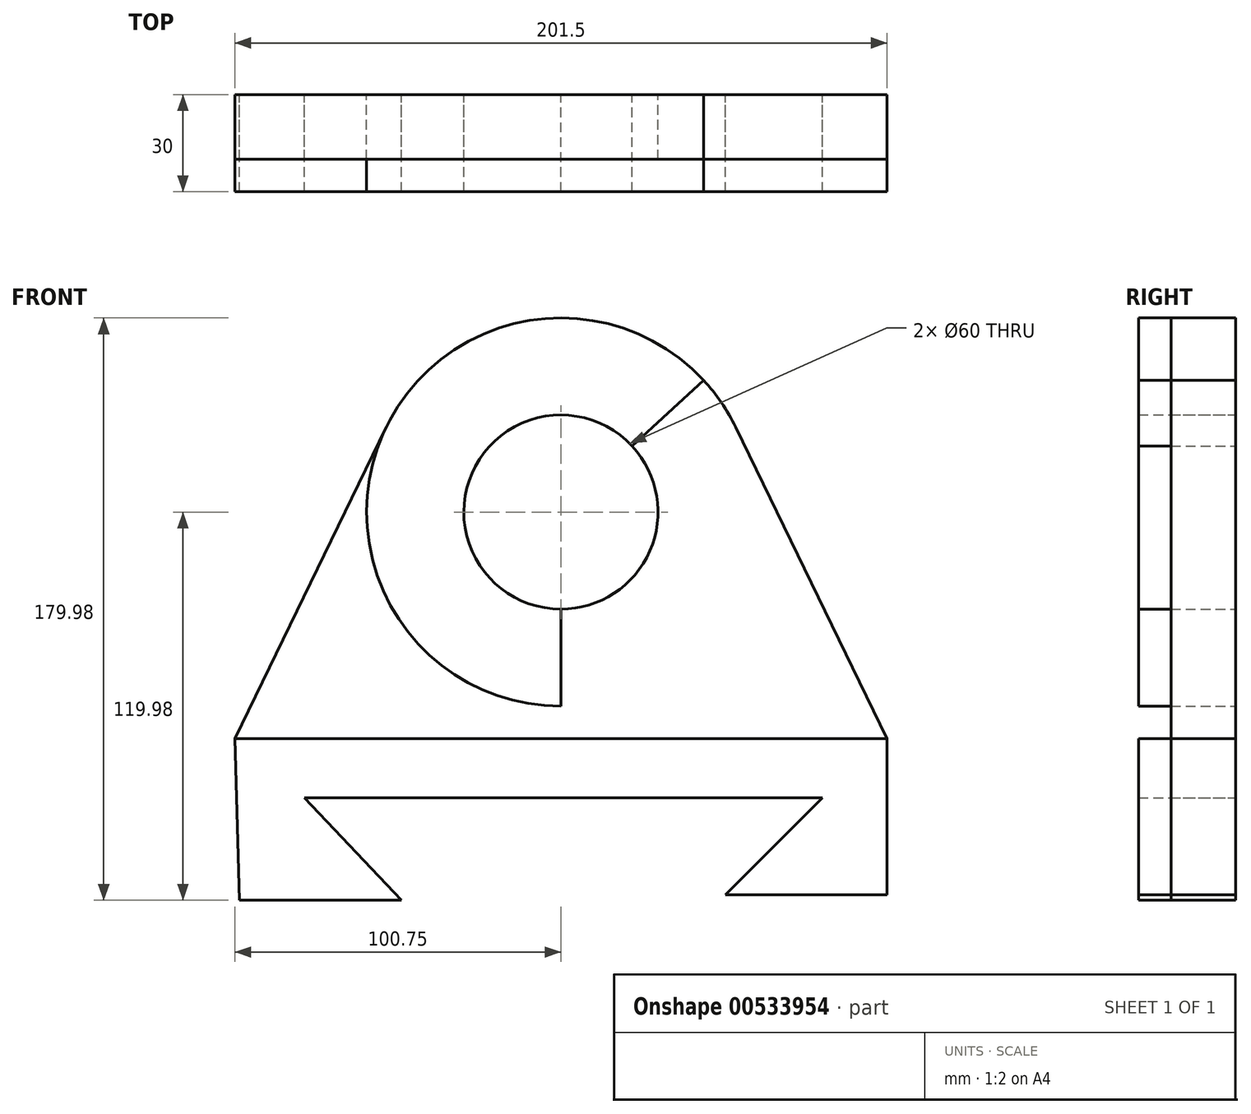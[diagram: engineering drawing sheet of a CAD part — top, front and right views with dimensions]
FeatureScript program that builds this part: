
annotation { "Feature Type Name" : "Feature", "Feature Type Description" : "" }
export const myFeature = defineFeature(function(context is Context, id is Id, definition is map)
    precondition{}
    {
        {
            var Q0;
            Q0=qCreatedBy(makeId("Front.planeOp"),FACE);
            var sketch = newSketch(context, id + "F0", { "sketchPlane" : qUnion([Q0])});
            skLineSegment(sketch, "E0", {"start": v(-100.75, 0) * mm, "end": v(100.75, 0) * mm});
            skLineSegment(sketch, "E1", {"start": v(100.75, 0) * mm, "end": v(100.75, -48.26) * mm});
            skLineSegment(sketch, "E2", {"start": v(100.75, -48.26) * mm, "end": v(50.75, -48.26) * mm});
            skLineSegment(sketch, "E3", {"start": v(-49.25, -49.98) * mm, "end": v(-99.25, -49.98) * mm});
            skLineSegment(sketch, "E4", {"start": v(-99.25, -49.98) * mm, "end": v(-100.75, 0) * mm});
            skCircle(sketch, "E5", {"center": v(0, 70) * mm, "radius": 30 * mm});
            skCircle(sketch, "E6", {"center": v(0, 70) * mm, "radius": 60 * mm});
            skLineSegment(sketch, "E7", {"start": v(0, 70) * mm, "end": v(0, 0) * mm});
            skLineSegment(sketch, "E8", {"start": v(0, 70) * mm, "end": v(44.09, 110.7) * mm});
            skLineSegment(sketch, "E9", {"start": v(44.09, 110.7) * mm, "end": v(0, 70) * mm});
            skLineSegment(sketch, "E10", {"start": v(0, 70) * mm, "end": v(-30, 70) * mm});
            skLineSegment(sketch, "E11", {"start": v(-49.25, -49.98) * mm, "end": v(-79.25, -18.26) * mm});
            skLineSegment(sketch, "E12", {"start": v(-79.25, -18.26) * mm, "end": v(80.75, -18.26) * mm});
            skLineSegment(sketch, "E13", {"start": v(80.75, -18.26) * mm, "end": v(50.75, -48.26) * mm});
            skLineSegment(sketch, "E14", {"start": v(-100.75, 0) * mm, "end": v(-53.96, 96.24) * mm});
            skLineSegment(sketch, "E15", {"start": v(53.96, 96.24) * mm, "end": v(100.75, 0) * mm});
            skSolve(sketch);
        }
        {
            var Q0;
            {var subQ0=sQuery(id+"F0.wireOp",EDGE,"E1");Q0=makeQuery(id+"F0.imprint","IMPRINT",FACE,{"disambiguationData":[TD([[makeQuery(id+"F0.imprint","IMPRINT",EDGE,{"derivedFrom":subQ0}),-1.0]])]});}
            var Q1;
            {var subQ4=sQuery(id+"F0.wireOp",EDGE,"E5");var subQ5=makeQuery(id+"F0.imprint","INTERSECT",VERTEX,{"derivedFrom":[subQ4,sQuery(id+"F0.wireOp",EDGE,"E10")]});Q1=makeQuery(id+"F0.imprint","IMPRINT",FACE,{"disambiguationData":[TD([[makeQuery(id+"F0.imprint","IMPRINT",EDGE,{"disambiguationData":[TD([[subQ5,1.0]])],"derivedFrom":subQ4}),-1.0]])]});}
            var Q2;
            {var subQ4=sQuery(id+"F0.wireOp",EDGE,"E5");var subQ6=sQuery(id+"F0.wireOp",EDGE,"E9");var subQ8=makeQuery(id+"F0.imprint","INTERSECT",VERTEX,{"derivedFrom":[subQ4,subQ6]});Q2=makeQuery(id+"F0.imprint","IMPRINT",FACE,{"disambiguationData":[TD([[makeQuery(id+"F0.imprint","IMPRINT",EDGE,{"disambiguationData":[TD([[subQ8,1.0]])],"derivedFrom":subQ4}),-1.0]])]});}
            extrude(context, id + "F1", {"entities" : qUnion([Q0, Q1, Q2]), "depth" : 30 * mm, "offsetDistance" : 25 * mm});
        }
        {
            var Q0;
            Q0 = qSketchRegion(id + "F0", true);
            extrude(context, id + "F2", {"entities" : qUnion([Q0]), "depth" : 20 * mm, "offsetDistance" : 25 * mm});
        }
    });
